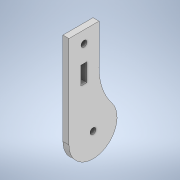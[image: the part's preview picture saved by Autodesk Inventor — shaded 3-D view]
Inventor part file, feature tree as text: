
AUTODESK INVENTOR PART (.ipt)
format: ipt  version: 2022 (Build 260153000, 153)  size: 124,928 bytes
history: native  units: mm
features: extrude x1, sketch x1
ambient origin geometry x8: Origin, YZ Plane, XZ Plane, XY Plane, X Axis, Y Axis, Z Axis, Center Point
bodies: Solid1 (feature_tree)
feature tree (2):
  extrude  "Extrusion1"  Depth=9.0mm
  sketch  "Sketch1"  dims[d9=58.0mm d14=3.0mm d15=0.0mm d18=9.0mm d19=3.0mm d20=6.0mm d21=7.5mm d22=3.0mm d23=15.0mm d24=12.0mm]
